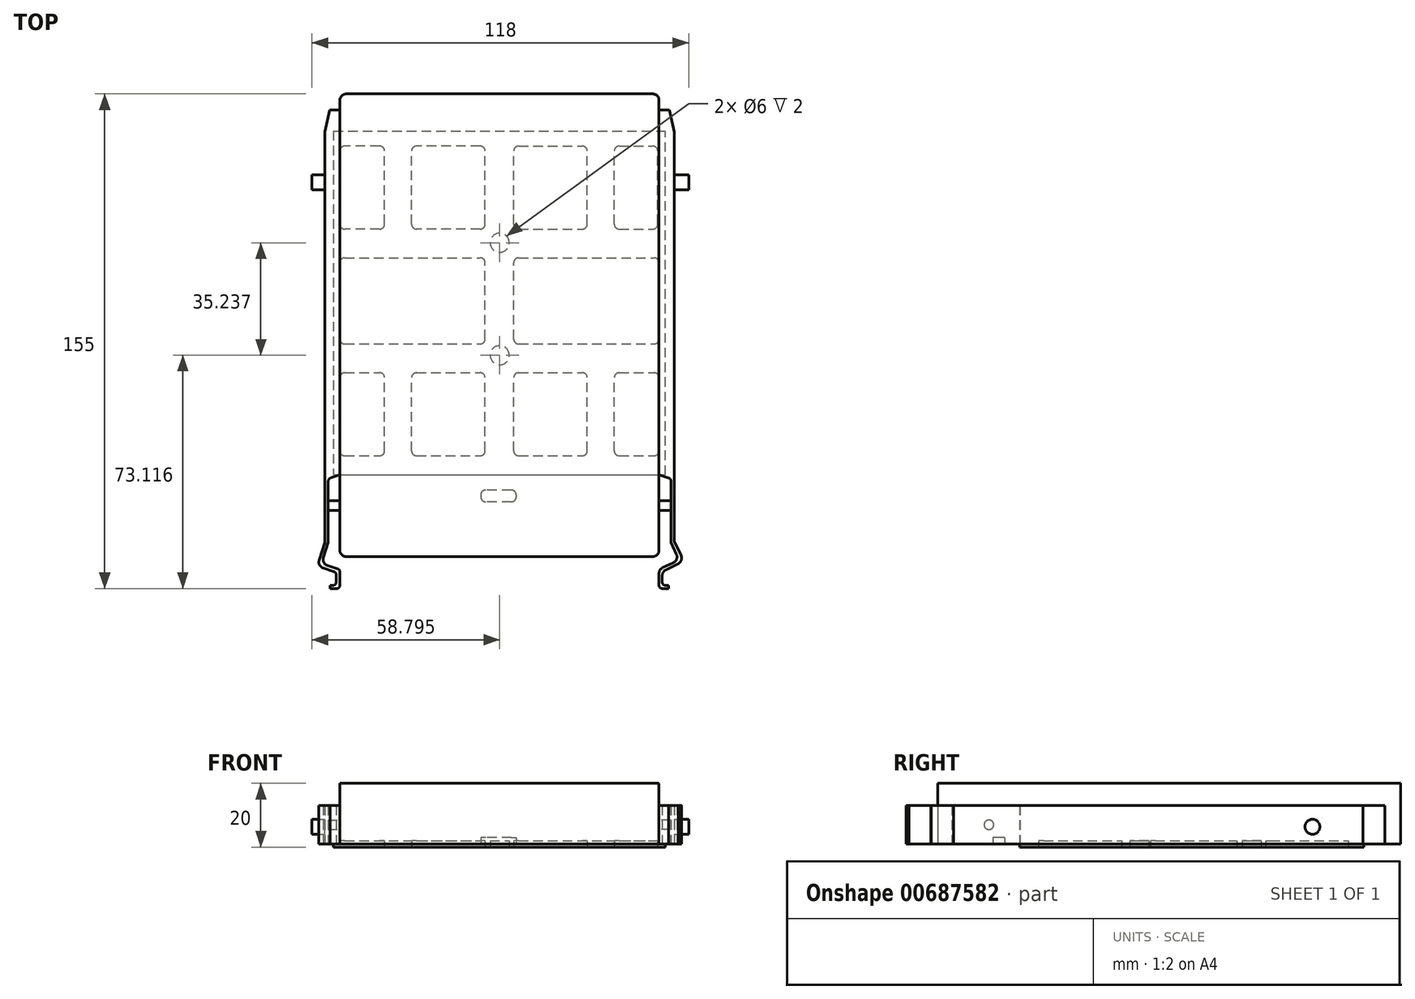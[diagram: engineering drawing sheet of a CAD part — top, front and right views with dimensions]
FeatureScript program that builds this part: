
annotation { "Feature Type Name" : "Feature", "Feature Type Description" : "" }
export const myFeature = defineFeature(function(context is Context, id is Id, definition is map)
    precondition{}
    {
        {
            var Q0;
            Q0=qCreatedBy(makeId("Top.planeOp"),FACE);
            var sketch = newSketch(context, id + "F0", { "sketchPlane" : qUnion([Q0])});
            skLineSegment(sketch, "E0.bottom", {"start": v(-53.24, 65.83) * mm, "end": v(42.76, 65.83) * mm});
            skLineSegment(sketch, "E0.top", {"start": v(-53.24, -79.17) * mm, "end": v(42.76, -79.17) * mm});
            skLineSegment(sketch, "E0.left", {"start": v(-55.24, 63.83) * mm, "end": v(-55.24, -77.17) * mm});
            skLineSegment(sketch, "E0.right", {"start": v(44.76, 63.83) * mm, "end": v(44.76, -77.17) * mm});
            skPoint(sketch, "E1.visualSharp", {"position": v(-55.24, 65.83) * mm});
            skArc(sketch, "E1.filletArc", {"start": v(-53.24, 65.83) * mm, "mid": v(-54.65, 65.24) * mm, "end": v(-55.24, 63.83) * mm});
            skPoint(sketch, "E2.visualSharp", {"position": v(44.76, 65.83) * mm});
            skArc(sketch, "E2.filletArc", {"start": v(44.76, 63.83) * mm, "mid": v(44.18, 65.24) * mm, "end": v(42.76, 65.83) * mm});
            skPoint(sketch, "E3.visualSharp", {"position": v(-55.24, -79.17) * mm});
            skArc(sketch, "E3.filletArc", {"start": v(-55.24, -77.17) * mm, "mid": v(-54.65, -78.59) * mm, "end": v(-53.24, -79.17) * mm});
            skPoint(sketch, "E4.visualSharp", {"position": v(44.76, -79.17) * mm});
            skArc(sketch, "E4.filletArc", {"start": v(42.76, -79.17) * mm, "mid": v(44.18, -78.59) * mm, "end": v(44.76, -77.17) * mm});
            skSolve(sketch);
        }
        {
            var Q0;
            Q0 = qSketchRegion(id + "F0", true);
            extrude(context, id + "F1", {"entities" : qUnion([Q0]), "depth" : 19 * mm, "offsetDistance" : 25 * mm});
        }
        {
            var Q0;
            Q0=makeQuery(id+"F1.opExtrude","SWEPT_FACE",FACE,{"disambiguationData":[OSD([sQuery(id+"F0.wireOp",EDGE,"E0.left")])]});
            var sketch = newSketch(context, id + "F2", { "sketchPlane" : qUnion([Q0])});
            skLineSegment(sketch, "E5", {"start": v(63.17, 0) * mm, "end": v(63.17, 6) * mm});
            skCircle(sketch, "E6", {"center": v(63.17, 6) * mm, "radius": 1.5 * mm});
            skSolve(sketch);
        }
        {
            var Q0;
            Q0 = qSketchRegion(id + "F2", true);
            extrude(context, id + "F3", {"entities" : qUnion([Q0]), "operationType" : NewBodyOperationType.ADD, "depth" : 4 * mm, "offsetDistance" : 25 * mm});
        }
        {
            var Q0;
            Q0=makeQuery(id+"F1.opExtrude","SWEPT_FACE",FACE,{"disambiguationData":[OSD([sQuery(id+"F0.wireOp",EDGE,"E0.right")])]});
            var sketch = newSketch(context, id + "F4", { "sketchPlane" : qUnion([Q0])});
            skLineSegment(sketch, "E7", {"start": v(-63.17, 19) * mm, "end": v(-63.17, 6) * mm});
            skCircle(sketch, "E8", {"center": v(-63.17, 6) * mm, "radius": 1.5 * mm});
            skSolve(sketch);
        }
        {
            var Q0;
            Q0 = qSketchRegion(id + "F4", true);
            extrude(context, id + "F5", {"entities" : qUnion([Q0]), "operationType" : NewBodyOperationType.ADD, "depth" : 4 * mm, "offsetDistance" : 25 * mm});
        }
        {
            var Q0;
            Q0=makeQuery(id+"F1.opExtrude","CAP_FACE",FACE,{"disambiguationData":[OSD([sQuery(id+"F0.wireOp",EDGE,"E0.bottom"),sQuery(id+"F0.wireOp",EDGE,"E0.top"),sQuery(id+"F0.wireOp",EDGE,"E0.left"),sQuery(id+"F0.wireOp",EDGE,"E0.right"),sQuery(id+"F0.wireOp",EDGE,"E1.filletArc"),sQuery(id+"F0.wireOp",EDGE,"E2.filletArc"),sQuery(id+"F0.wireOp",EDGE,"E3.filletArc"),sQuery(id+"F0.wireOp",EDGE,"E4.filletArc")])],"isStart":true});
            var sketch = newSketch(context, id + "F6", { "sketchPlane" : qUnion([Q0])});
            skLineSegment(sketch, "E9", {"start": v(44.76, 84.43) * mm, "end": v(44.76, 89.17) * mm});
            skLineSegment(sketch, "E10", {"start": v(45.76, 89.17) * mm, "end": v(47.76, 89.17) * mm});
            skLineSegment(sketch, "E11", {"start": v(44.76, 88.17) * mm, "end": v(44.76, 84.43) * mm});
            skPoint(sketch, "E12.visualSharp", {"position": v(44.76, 89.17) * mm});
            skArc(sketch, "E12.filletArc", {"start": v(45.76, 89.17) * mm, "mid": v(45.05, 88.88) * mm, "end": v(44.76, 88.17) * mm});
            skLineSegment(sketch, "E13", {"start": v(45.9, 82.63) * mm, "end": v(49.27, 81.02) * mm});
            skPoint(sketch, "E14.visualSharp", {"position": v(44.76, 83.17) * mm});
            skArc(sketch, "E14.filletArc", {"start": v(44.76, 84.43) * mm, "mid": v(45.07, 83.37) * mm, "end": v(45.9, 82.63) * mm});
            skLineSegment(sketch, "E15", {"start": v(50.21, 78.35) * mm, "end": v(48.49, 74.74) * mm});
            skPoint(sketch, "E15.endSnap0", {"position": v(48.49, 81.4) * mm});
            skPoint(sketch, "E16.visualSharp", {"position": v(51.08, 80.15) * mm});
            skArc(sketch, "E16.filletArc", {"start": v(50.21, 78.35) * mm, "mid": v(50.3, 79.88) * mm, "end": v(49.27, 81.02) * mm});
            skLineSegment(sketch, "E17", {"start": v(47.76, 89.17) * mm, "end": v(47.76, 88.17) * mm});
            skLineSegment(sketch, "E18", {"start": v(47.76, 88.17) * mm, "end": v(46.76, 88.17) * mm});
            skLineSegment(sketch, "E19", {"start": v(45.76, 85.1) * mm, "end": v(45.76, 87.17) * mm});
            skLineSegment(sketch, "E20", {"start": v(45.76, 84.43) * mm, "end": v(45.76, 83.87) * mm});
            skLineSegment(sketch, "E21", {"start": v(46.88, 83.32) * mm, "end": v(51.08, 81.24) * mm});
            skArc(sketch, "E22.filletArc", {"start": v(46.76, 88.17) * mm, "mid": v(46.05, 87.88) * mm, "end": v(45.76, 87.17) * mm});
            skPoint(sketch, "E23.newPointB", {"position": v(45.76, 84.43) * mm});
            skArc(sketch, "E23.filletArc", {"start": v(45.76, 85.1) * mm, "mid": v(46.06, 84.05) * mm, "end": v(46.88, 83.32) * mm});
            skLineSegment(sketch, "E24", {"start": v(49.49, 74.3) * mm, "end": v(51.63, 78.78) * mm});
            skLineSegment(sketch, "E25", {"start": v(51.08, 81.24) * mm, "end": v(50.75, 81.41) * mm});
            skPoint(sketch, "E26.visualSharp", {"position": v(52.46, 80.52) * mm});
            skArc(sketch, "E26.filletArc", {"start": v(51.63, 78.78) * mm, "mid": v(51.72, 80.27) * mm, "end": v(50.75, 81.41) * mm});
            skLineSegment(sketch, "E27", {"start": v(48.49, 74.74) * mm, "end": v(48.49, 55.46) * mm});
            skLineSegment(sketch, "E28", {"start": v(49.49, 74.3) * mm, "end": v(49.49, 54.74) * mm});
            skPoint(sketch, "E29.orphan", {"position": v(44.76, 77.17) * mm});
            skPoint(sketch, "E30", {"position": v(44.76, 54.67) * mm});
            skLineSegment(sketch, "E31", {"start": v(47.81, 54.5) * mm, "end": v(44.76, 53.47) * mm});
            skPoint(sketch, "E32.visualSharp", {"position": v(48.49, 54.74) * mm});
            skArc(sketch, "E32.filletArc", {"start": v(47.81, 54.5) * mm, "mid": v(48.3, 54.87) * mm, "end": v(48.49, 55.46) * mm});
            skLineSegment(sketch, "E33", {"start": v(49.49, 54.74) * mm, "end": v(49.49, -53.99) * mm});
            skLineSegment(sketch, "E34", {"start": v(47.99, -60.83) * mm, "end": v(44.76, -60.83) * mm});
            skLineSegment(sketch, "E35", {"start": v(47.99, -60.83) * mm, "end": v(49.49, -53.99) * mm});
            skPoint(sketch, "E36.orphan", {"position": v(49.49, -60.83) * mm});
            skSolve(sketch);
        }
        {
            var Q0;
            Q0 = qSketchRegion(id + "F6", true);
            var Q1;
            Q1=makeQuery(id+"F6.imprint","IMPRINT",FACE,{"disambiguationData":[TD([[makeQuery(id+"F6.imprint","IMPRINT",EDGE,{"derivedFrom":sQuery(id+"F6.wireOp",EDGE,"E10")}),-1.0]])]});
            extrude(context, id + "F7", {"entities" : qUnion([Q0, Q1]), "oppositeDirection" : true, "depth" : 12 * mm, "offsetDistance" : 25 * mm});
        }
        {
            var Q0;
            Q0 = qSketchRegion(id + "F2", true);
            extrude(context, id + "F8", {"entities" : qUnion([Q0]), "operationType" : NewBodyOperationType.ADD, "depth" : 4 * mm, "offsetDistance" : 25 * mm});
        }
        {
            var Q0;
            Q0=makeQuery(id+"F1.opExtrude","CAP_FACE",FACE,{"disambiguationData":[OSD([sQuery(id+"F0.wireOp",EDGE,"E0.bottom"),sQuery(id+"F0.wireOp",EDGE,"E0.top"),sQuery(id+"F0.wireOp",EDGE,"E0.left"),sQuery(id+"F0.wireOp",EDGE,"E0.right"),sQuery(id+"F0.wireOp",EDGE,"E1.filletArc"),sQuery(id+"F0.wireOp",EDGE,"E2.filletArc"),sQuery(id+"F0.wireOp",EDGE,"E3.filletArc"),sQuery(id+"F0.wireOp",EDGE,"E4.filletArc")])],"isStart":true});
            var sketch = newSketch(context, id + "F9", { "sketchPlane" : qUnion([Q0])});
            skLineSegment(sketch, "E37", {"start": v(-52.1, -65.83) * mm, "end": v(-52.1, -60.83) * mm});
            skLineSegment(sketch, "E38", {"start": v(-55.24, -60.83) * mm, "end": v(-58.46, -60.83) * mm});
            skLineSegment(sketch, "E39", {"start": v(-58.46, -60.83) * mm, "end": v(-59.96, -53.99) * mm});
            skLineSegment(sketch, "E40", {"start": v(-59.96, -53.99) * mm, "end": v(-59.96, 74.73) * mm});
            skLineSegment(sketch, "E41", {"start": v(-58.96, 74.73) * mm, "end": v(-58.96, 55.82) * mm});
            skLineSegment(sketch, "E42", {"start": v(-57.92, 54.4) * mm, "end": v(-55.24, 53.53) * mm});
            skPoint(sketch, "E43.visualSharp", {"position": v(-58.96, 54.73) * mm});
            skArc(sketch, "E43.filletArc", {"start": v(-58.96, 55.82) * mm, "mid": v(-58.68, 54.94) * mm, "end": v(-57.92, 54.4) * mm});
            skPoint(sketch, "E44.start.orphan", {"position": v(-58.96, 83.95) * mm});
            skPoint(sketch, "E45", {"position": v(44.69, 89.17) * mm});
            skLineSegment(sketch, "E46", {"start": v(-55.24, 83.17) * mm, "end": v(-55.24, 89.17) * mm});
            skPoint(sketch, "E47.end.orphan", {"position": v(-53.24, 89.17) * mm});
            skLineSegment(sketch, "E48", {"start": v(-56.24, 89.17) * mm, "end": v(-58.24, 89.17) * mm});
            skLineSegment(sketch, "E49", {"start": v(-55.24, 88.17) * mm, "end": v(-55.24, 83.92) * mm});
            skLineSegment(sketch, "E50", {"start": v(-58.96, 74.73) * mm, "end": v(-60.4, 79.52) * mm});
            skLineSegment(sketch, "E51", {"start": v(-59.07, 82.01) * mm, "end": v(-55.95, 82.96) * mm});
            skLineSegment(sketch, "E52", {"start": v(-59.96, 74.73) * mm, "end": v(-61.73, 80.25) * mm});
            skLineSegment(sketch, "E53", {"start": v(-60.43, 82.77) * mm, "end": v(-57.1, 83.83) * mm});
            skLineSegment(sketch, "E54", {"start": v(-56.4, 84.79) * mm, "end": v(-56.4, 87.17) * mm});
            skLineSegment(sketch, "E55", {"start": v(-57.4, 88.17) * mm, "end": v(-58.24, 88.17) * mm});
            skLineSegment(sketch, "E56", {"start": v(-58.24, 88.17) * mm, "end": v(-58.24, 89.17) * mm});
            skPoint(sketch, "E57.orphan", {"position": v(-55.24, 77.17) * mm});
            skPoint(sketch, "E58.visualSharp", {"position": v(-55.24, 89.17) * mm});
            skArc(sketch, "E58.filletArc", {"start": v(-55.24, 88.17) * mm, "mid": v(-55.53, 88.88) * mm, "end": v(-56.24, 89.17) * mm});
            skPoint(sketch, "E59.visualSharp", {"position": v(-56.4, 88.17) * mm});
            skArc(sketch, "E59.filletArc", {"start": v(-56.4, 87.17) * mm, "mid": v(-56.7, 87.88) * mm, "end": v(-57.4, 88.17) * mm});
            skPoint(sketch, "E60.visualSharp", {"position": v(-56.4, 84.05) * mm});
            skArc(sketch, "E60.filletArc", {"start": v(-57.1, 83.83) * mm, "mid": v(-56.6, 84.2) * mm, "end": v(-56.4, 84.79) * mm});
            skPoint(sketch, "E61.visualSharp", {"position": v(-55.24, 83.17) * mm});
            skArc(sketch, "E61.filletArc", {"start": v(-55.95, 82.96) * mm, "mid": v(-55.43, 83.32) * mm, "end": v(-55.24, 83.92) * mm});
            skPoint(sketch, "E62.visualSharp", {"position": v(-60.98, 81.43) * mm});
            skArc(sketch, "E62.filletArc", {"start": v(-59.07, 82.01) * mm, "mid": v(-60.25, 81.04) * mm, "end": v(-60.4, 79.52) * mm});
            skPoint(sketch, "E63.visualSharp", {"position": v(-62.34, 82.16) * mm});
            skArc(sketch, "E63.filletArc", {"start": v(-60.43, 82.77) * mm, "mid": v(-61.6, 81.78) * mm, "end": v(-61.73, 80.25) * mm});
            skSolve(sketch);
        }
        {
            var Q0;
            Q0 = qSketchRegion(id + "F9", true);
            var Q1;
            {var subQ0=sQuery(id+"F9.wireOp",EDGE,"E38");Q1=makeQuery(id+"F9.imprint","IMPRINT",FACE,{"disambiguationData":[TD([[makeQuery(id+"F9.imprint","IMPRINT",EDGE,{"derivedFrom":subQ0}),-1.0]])]});}
            extrude(context, id + "F10", {"entities" : qUnion([Q0, Q1]), "oppositeDirection" : true, "depth" : 12 * mm, "offsetDistance" : 25 * mm});
        }
        {
            var Q0;
            Q0=makeQuery(id+"F1.opExtrude","CAP_FACE",FACE,{"disambiguationData":[OSD([sQuery(id+"F0.wireOp",EDGE,"E0.bottom"),sQuery(id+"F0.wireOp",EDGE,"E0.top"),sQuery(id+"F0.wireOp",EDGE,"E0.left"),sQuery(id+"F0.wireOp",EDGE,"E0.right"),sQuery(id+"F0.wireOp",EDGE,"E1.filletArc"),sQuery(id+"F0.wireOp",EDGE,"E2.filletArc"),sQuery(id+"F0.wireOp",EDGE,"E3.filletArc"),sQuery(id+"F0.wireOp",EDGE,"E4.filletArc")])],"isStart":true});
            var sketch = newSketch(context, id + "F11", { "sketchPlane" : qUnion([Q0])});
            skLineSegment(sketch, "E64", {"start": v(44.76, 53.57) * mm, "end": v(44.76, -54.23) * mm});
            skLineSegment(sketch, "E65", {"start": v(44.76, -54.23) * mm, "end": v(-55.24, -54.23) * mm});
            skLineSegment(sketch, "E66", {"start": v(-55.24, -54.23) * mm, "end": v(-57.24, -54.23) * mm});
            skLineSegment(sketch, "E67", {"start": v(44.76, -54.23) * mm, "end": v(46.76, -54.23) * mm});
            skPoint(sketch, "E68", {"position": v(-55.24, 53.54) * mm});
            skLineSegment(sketch, "E69", {"start": v(-57.24, -54.23) * mm, "end": v(-57.24, 53.54) * mm});
            skLineSegment(sketch, "E70", {"start": v(-57.24, 53.54) * mm, "end": v(46.76, 53.54) * mm});
            skLineSegment(sketch, "E71", {"start": v(46.76, 53.54) * mm, "end": v(46.76, -54.23) * mm});
            skSolve(sketch);
        }
        {
            var Q0;
            Q0 = qSketchRegion(id + "F11", true);
            extrude(context, id + "F12", {"entities" : qUnion([Q0]), "operationType" : NewBodyOperationType.ADD, "depth" : 1 * mm, "offsetDistance" : 25 * mm});
        }
        {
            var Q0;
            Q0=makeQuery(id+"F12.opExtrude","CAP_FACE",FACE,{"disambiguationData":[OSD([sQuery(id+"F11.wireOp",EDGE,"E65"),sQuery(id+"F11.wireOp",EDGE,"E66"),sQuery(id+"F11.wireOp",EDGE,"E67"),sQuery(id+"F11.wireOp",EDGE,"E69"),sQuery(id+"F11.wireOp",EDGE,"E70"),sQuery(id+"F11.wireOp",EDGE,"E71")])],"isStart":false});
            var sketch = newSketch(context, id + "F13", { "sketchPlane" : qUnion([Q0])});
            skLineSegment(sketch, "E72.bottom", {"start": v(-53.74, 47.54) * mm, "end": v(-42.74, 47.54) * mm});
            skLineSegment(sketch, "E72.top", {"start": v(-53.74, 21.54) * mm, "end": v(-42.74, 21.54) * mm});
            skLineSegment(sketch, "E72.left", {"start": v(-55.24, 46.04) * mm, "end": v(-55.24, 23.04) * mm});
            skLineSegment(sketch, "E72.right", {"start": v(-41.24, 46.04) * mm, "end": v(-41.24, 23.04) * mm});
            skPoint(sketch, "E73", {"position": v(-51.73, 53.54) * mm});
            skPoint(sketch, "E74.visualSharp", {"position": v(-55.24, 47.54) * mm});
            skArc(sketch, "E74.filletArc", {"start": v(-53.74, 47.54) * mm, "mid": v(-54.8, 47.1) * mm, "end": v(-55.24, 46.04) * mm});
            skPoint(sketch, "E75.visualSharp", {"position": v(-41.24, 47.54) * mm});
            skArc(sketch, "E75.filletArc", {"start": v(-41.24, 46.04) * mm, "mid": v(-41.68, 47.1) * mm, "end": v(-42.74, 47.54) * mm});
            skPoint(sketch, "E76.visualSharp", {"position": v(-41.24, 21.54) * mm});
            skArc(sketch, "E76.filletArc", {"start": v(-42.74, 21.54) * mm, "mid": v(-41.68, 21.98) * mm, "end": v(-41.24, 23.04) * mm});
            skPoint(sketch, "E77.visualSharp", {"position": v(-55.24, 21.54) * mm});
            skArc(sketch, "E77.filletArc", {"start": v(-55.24, 23.04) * mm, "mid": v(-54.8, 21.98) * mm, "end": v(-53.74, 21.54) * mm});
            skSolve(sketch);
        }
        {
            var Q0;
            Q0 = qSketchRegion(id + "F13", true);
            extrude(context, id + "F14", {"entities" : qUnion([Q0]), "operationType" : NewBodyOperationType.REMOVE, "oppositeDirection" : true, "depth" : 2 * mm, "offsetDistance" : 25 * mm});
        }
        {
            var Q0;
            Q0=makeQuery(id+"F12.opExtrude","CAP_FACE",FACE,{"disambiguationData":[OSD([sQuery(id+"F11.wireOp",EDGE,"E65"),sQuery(id+"F11.wireOp",EDGE,"E66"),sQuery(id+"F11.wireOp",EDGE,"E67"),sQuery(id+"F11.wireOp",EDGE,"E69"),sQuery(id+"F11.wireOp",EDGE,"E70"),sQuery(id+"F11.wireOp",EDGE,"E71")])],"isStart":false});
            var sketch = newSketch(context, id + "F15", { "sketchPlane" : qUnion([Q0])});
            skLineSegment(sketch, "E78.bottom", {"start": v(-31.24, 47.54) * mm, "end": v(-11.24, 47.54) * mm});
            skLineSegment(sketch, "E78.top", {"start": v(-31.24, 21.54) * mm, "end": v(-11.24, 21.54) * mm});
            skLineSegment(sketch, "E78.left", {"start": v(-32.74, 46.04) * mm, "end": v(-32.74, 23.04) * mm});
            skLineSegment(sketch, "E78.right", {"start": v(-9.74, 46.04) * mm, "end": v(-9.74, 23.04) * mm});
            skPoint(sketch, "E79.visualSharp", {"position": v(-32.74, 47.54) * mm});
            skArc(sketch, "E79.filletArc", {"start": v(-31.24, 47.54) * mm, "mid": v(-32.3, 47.1) * mm, "end": v(-32.74, 46.04) * mm});
            skPoint(sketch, "E80.visualSharp", {"position": v(-9.74, 47.54) * mm});
            skArc(sketch, "E80.filletArc", {"start": v(-9.74, 46.04) * mm, "mid": v(-10.18, 47.1) * mm, "end": v(-11.24, 47.54) * mm});
            skPoint(sketch, "E81.visualSharp", {"position": v(-9.74, 21.54) * mm});
            skArc(sketch, "E81.filletArc", {"start": v(-11.24, 21.54) * mm, "mid": v(-10.18, 21.98) * mm, "end": v(-9.74, 23.04) * mm});
            skPoint(sketch, "E82.visualSharp", {"position": v(-32.74, 21.54) * mm});
            skArc(sketch, "E82.filletArc", {"start": v(-32.74, 23.04) * mm, "mid": v(-32.3, 21.98) * mm, "end": v(-31.24, 21.54) * mm});
            skSolve(sketch);
        }
        {
            var Q0;
            Q0 = qSketchRegion(id + "F15", true);
            extrude(context, id + "F16", {"entities" : qUnion([Q0]), "operationType" : NewBodyOperationType.REMOVE, "oppositeDirection" : true, "depth" : 2 * mm, "offsetDistance" : 25 * mm});
        }
        {
            var Q0;
            Q0=makeQuery(id+"F12.opExtrude","CAP_FACE",FACE,{"disambiguationData":[OSD([sQuery(id+"F11.wireOp",EDGE,"E65"),sQuery(id+"F11.wireOp",EDGE,"E66"),sQuery(id+"F11.wireOp",EDGE,"E67"),sQuery(id+"F11.wireOp",EDGE,"E69"),sQuery(id+"F11.wireOp",EDGE,"E70"),sQuery(id+"F11.wireOp",EDGE,"E71")])],"isStart":false});
            var sketch = newSketch(context, id + "F17", { "sketchPlane" : qUnion([Q0])});
            skLineSegment(sketch, "E83.bottom", {"start": v(0.76, 47.54) * mm, "end": v(20.76, 47.54) * mm});
            skLineSegment(sketch, "E83.top", {"start": v(0.76, 21.54) * mm, "end": v(20.76, 21.54) * mm});
            skLineSegment(sketch, "E83.left", {"start": v(-0.74, 46.04) * mm, "end": v(-0.74, 23.04) * mm});
            skLineSegment(sketch, "E83.right", {"start": v(22.26, 46.04) * mm, "end": v(22.26, 23.04) * mm});
            skPoint(sketch, "E84.visualSharp", {"position": v(-0.74, 47.54) * mm});
            skArc(sketch, "E84.filletArc", {"start": v(0.76, 47.54) * mm, "mid": v(-0.3, 47.1) * mm, "end": v(-0.74, 46.04) * mm});
            skPoint(sketch, "E85.visualSharp", {"position": v(22.26, 47.54) * mm});
            skArc(sketch, "E85.filletArc", {"start": v(22.26, 46.04) * mm, "mid": v(21.82, 47.1) * mm, "end": v(20.76, 47.54) * mm});
            skPoint(sketch, "E86.visualSharp", {"position": v(22.26, 21.54) * mm});
            skArc(sketch, "E86.filletArc", {"start": v(20.76, 21.54) * mm, "mid": v(21.82, 21.98) * mm, "end": v(22.26, 23.04) * mm});
            skPoint(sketch, "E87.visualSharp", {"position": v(-0.74, 21.54) * mm});
            skArc(sketch, "E87.filletArc", {"start": v(-0.74, 23.04) * mm, "mid": v(-0.3, 21.98) * mm, "end": v(0.76, 21.54) * mm});
            skSolve(sketch);
        }
        {
            var Q0;
            Q0 = qSketchRegion(id + "F17", true);
            extrude(context, id + "F18", {"entities" : qUnion([Q0]), "operationType" : NewBodyOperationType.REMOVE, "oppositeDirection" : true, "depth" : 2 * mm, "offsetDistance" : 25 * mm});
        }
        {
            var Q0;
            Q0=makeQuery(id+"F12.opExtrude","CAP_FACE",FACE,{"disambiguationData":[OSD([sQuery(id+"F11.wireOp",EDGE,"E65"),sQuery(id+"F11.wireOp",EDGE,"E66"),sQuery(id+"F11.wireOp",EDGE,"E67"),sQuery(id+"F11.wireOp",EDGE,"E69"),sQuery(id+"F11.wireOp",EDGE,"E70"),sQuery(id+"F11.wireOp",EDGE,"E71")])],"isStart":false});
            var sketch = newSketch(context, id + "F19", { "sketchPlane" : qUnion([Q0])});
            skLineSegment(sketch, "E88.bottom", {"start": v(32.26, 47.54) * mm, "end": v(43.26, 47.54) * mm});
            skLineSegment(sketch, "E88.top", {"start": v(32.26, 21.54) * mm, "end": v(43.26, 21.54) * mm});
            skLineSegment(sketch, "E88.left", {"start": v(30.76, 46.04) * mm, "end": v(30.76, 23.04) * mm});
            skLineSegment(sketch, "E88.right", {"start": v(44.76, 46.04) * mm, "end": v(44.76, 23.04) * mm});
            skPoint(sketch, "E89.visualSharp", {"position": v(30.76, 47.54) * mm});
            skArc(sketch, "E89.filletArc", {"start": v(32.26, 47.54) * mm, "mid": v(31.2, 47.1) * mm, "end": v(30.76, 46.04) * mm});
            skPoint(sketch, "E90.visualSharp", {"position": v(44.76, 47.54) * mm});
            skArc(sketch, "E90.filletArc", {"start": v(44.76, 46.04) * mm, "mid": v(44.32, 47.1) * mm, "end": v(43.26, 47.54) * mm});
            skPoint(sketch, "E91.visualSharp", {"position": v(30.76, 21.54) * mm});
            skArc(sketch, "E91.filletArc", {"start": v(30.76, 23.04) * mm, "mid": v(31.2, 21.98) * mm, "end": v(32.26, 21.54) * mm});
            skPoint(sketch, "E92.visualSharp", {"position": v(44.76, 21.54) * mm});
            skArc(sketch, "E92.filletArc", {"start": v(43.26, 21.54) * mm, "mid": v(44.32, 21.98) * mm, "end": v(44.76, 23.04) * mm});
            skSolve(sketch);
        }
        {
            var Q0;
            Q0 = qSketchRegion(id + "F19", true);
            extrude(context, id + "F20", {"entities" : qUnion([Q0]), "operationType" : NewBodyOperationType.REMOVE, "oppositeDirection" : true, "depth" : 2 * mm, "offsetDistance" : 25 * mm});
        }
        {
            var Q0;
            Q0=makeQuery(id+"F12.opExtrude","CAP_FACE",FACE,{"disambiguationData":[OSD([sQuery(id+"F11.wireOp",EDGE,"E65"),sQuery(id+"F11.wireOp",EDGE,"E66"),sQuery(id+"F11.wireOp",EDGE,"E67"),sQuery(id+"F11.wireOp",EDGE,"E69"),sQuery(id+"F11.wireOp",EDGE,"E70"),sQuery(id+"F11.wireOp",EDGE,"E71")])],"isStart":false});
            var sketch = newSketch(context, id + "F21", { "sketchPlane" : qUnion([Q0])});
            skPoint(sketch, "E93.oppositeSnap0", {"position": v(-12.3, 24.1) * mm});
            skPoint(sketch, "E94.visualSharp", {"position": v(-55.24, 12.54) * mm});
            skPoint(sketch, "E95.visualSharp", {"position": v(-12.3, 12.54) * mm});
            skPoint(sketch, "E96.visualSharp", {"position": v(-12.3, -14.46) * mm});
            skPoint(sketch, "E97.visualSharp", {"position": v(-55.24, -14.46) * mm});
            skLineSegment(sketch, "E98.bottom", {"start": v(-53.74, 12.54) * mm, "end": v(-11.24, 12.54) * mm});
            skLineSegment(sketch, "E98.top", {"start": v(-53.74, -14.47) * mm, "end": v(-11.24, -14.47) * mm});
            skLineSegment(sketch, "E98.left", {"start": v(-55.24, 11.04) * mm, "end": v(-55.24, -12.97) * mm});
            skLineSegment(sketch, "E98.right", {"start": v(-9.74, 11.04) * mm, "end": v(-9.74, -12.97) * mm});
            skArc(sketch, "E99.filletArc", {"start": v(-53.74, 12.54) * mm, "mid": v(-54.8, 12.1) * mm, "end": v(-55.24, 11.04) * mm});
            skPoint(sketch, "E100.visualSharp", {"position": v(-9.74, 12.54) * mm});
            skArc(sketch, "E100.filletArc", {"start": v(-9.74, 11.04) * mm, "mid": v(-10.18, 12.1) * mm, "end": v(-11.24, 12.54) * mm});
            skPoint(sketch, "E101.visualSharp", {"position": v(-9.74, -14.47) * mm});
            skArc(sketch, "E101.filletArc", {"start": v(-11.24, -14.47) * mm, "mid": v(-10.18, -14.03) * mm, "end": v(-9.74, -12.97) * mm});
            skPoint(sketch, "E102.visualSharp", {"position": v(-55.24, -14.47) * mm});
            skArc(sketch, "E102.filletArc", {"start": v(-55.24, -12.97) * mm, "mid": v(-54.8, -14.03) * mm, "end": v(-53.74, -14.47) * mm});
            skSolve(sketch);
        }
        {
            var Q0;
            Q0 = qSketchRegion(id + "F21", true);
            extrude(context, id + "F22", {"entities" : qUnion([Q0]), "operationType" : NewBodyOperationType.REMOVE, "oppositeDirection" : true, "depth" : 2 * mm, "offsetDistance" : 25 * mm});
        }
        {
            var Q0;
            Q0=makeQuery(id+"F12.opExtrude","CAP_FACE",FACE,{"disambiguationData":[OSD([sQuery(id+"F11.wireOp",EDGE,"E65"),sQuery(id+"F11.wireOp",EDGE,"E66"),sQuery(id+"F11.wireOp",EDGE,"E67"),sQuery(id+"F11.wireOp",EDGE,"E69"),sQuery(id+"F11.wireOp",EDGE,"E70"),sQuery(id+"F11.wireOp",EDGE,"E71")])],"isStart":false});
            var sketch = newSketch(context, id + "F23", { "sketchPlane" : qUnion([Q0])});
            skLineSegment(sketch, "E103.bottom", {"start": v(0.76, 12.54) * mm, "end": v(43.26, 12.54) * mm});
            skLineSegment(sketch, "E103.top", {"start": v(0.76, -14.46) * mm, "end": v(43.26, -14.46) * mm});
            skLineSegment(sketch, "E103.left", {"start": v(-0.74, 11.04) * mm, "end": v(-0.74, -12.96) * mm});
            skLineSegment(sketch, "E103.right", {"start": v(44.76, 11.04) * mm, "end": v(44.76, -12.96) * mm});
            skPoint(sketch, "E104.visualSharp", {"position": v(-0.74, 12.54) * mm});
            skArc(sketch, "E104.filletArc", {"start": v(0.76, 12.54) * mm, "mid": v(-0.3, 12.1) * mm, "end": v(-0.74, 11.04) * mm});
            skPoint(sketch, "E105.visualSharp", {"position": v(-0.74, -14.46) * mm});
            skArc(sketch, "E105.filletArc", {"start": v(-0.74, -12.96) * mm, "mid": v(-0.3, -14.02) * mm, "end": v(0.76, -14.46) * mm});
            skPoint(sketch, "E106.visualSharp", {"position": v(44.76, 12.54) * mm});
            skArc(sketch, "E106.filletArc", {"start": v(44.76, 11.04) * mm, "mid": v(44.32, 12.1) * mm, "end": v(43.26, 12.54) * mm});
            skPoint(sketch, "E107.visualSharp", {"position": v(44.76, -14.46) * mm});
            skArc(sketch, "E107.filletArc", {"start": v(43.26, -14.46) * mm, "mid": v(44.32, -14.02) * mm, "end": v(44.76, -12.96) * mm});
            skSolve(sketch);
        }
        {
            var Q0;
            Q0 = qSketchRegion(id + "F23", true);
            extrude(context, id + "F24", {"entities" : qUnion([Q0]), "operationType" : NewBodyOperationType.REMOVE, "oppositeDirection" : true, "depth" : 2 * mm, "offsetDistance" : 25 * mm});
        }
        {
            var Q0;
            Q0=makeQuery(id+"F12.opExtrude","CAP_FACE",FACE,{"disambiguationData":[OSD([sQuery(id+"F11.wireOp",EDGE,"E65"),sQuery(id+"F11.wireOp",EDGE,"E66"),sQuery(id+"F11.wireOp",EDGE,"E67"),sQuery(id+"F11.wireOp",EDGE,"E69"),sQuery(id+"F11.wireOp",EDGE,"E70"),sQuery(id+"F11.wireOp",EDGE,"E71")])],"isStart":false});
            var sketch = newSketch(context, id + "F25", { "sketchPlane" : qUnion([Q0])});
            skPoint(sketch, "E108.firstSnap0", {"position": v(-9.74, -9.02) * mm});
            skPoint(sketch, "E108.oppositeSnap0", {"position": v(-32.74, 12.68) * mm});
            skLineSegment(sketch, "E108.bottom", {"start": v(-11.24, -23.47) * mm, "end": v(-31.24, -23.47) * mm});
            skLineSegment(sketch, "E108.top", {"start": v(-11.24, -49.47) * mm, "end": v(-31.24, -49.47) * mm});
            skLineSegment(sketch, "E108.left", {"start": v(-9.74, -24.97) * mm, "end": v(-9.74, -47.97) * mm});
            skLineSegment(sketch, "E108.right", {"start": v(-32.74, -24.97) * mm, "end": v(-32.74, -47.97) * mm});
            skPoint(sketch, "E109.visualSharp", {"position": v(-32.74, -23.47) * mm});
            skArc(sketch, "E109.filletArc", {"start": v(-31.24, -23.47) * mm, "mid": v(-32.3, -23.91) * mm, "end": v(-32.74, -24.97) * mm});
            skPoint(sketch, "E110.visualSharp", {"position": v(-9.74, -23.47) * mm});
            skArc(sketch, "E110.filletArc", {"start": v(-9.74, -24.97) * mm, "mid": v(-10.18, -23.91) * mm, "end": v(-11.24, -23.47) * mm});
            skPoint(sketch, "E111.visualSharp", {"position": v(-32.74, -49.47) * mm});
            skArc(sketch, "E111.filletArc", {"start": v(-32.74, -47.97) * mm, "mid": v(-32.3, -49.03) * mm, "end": v(-31.24, -49.47) * mm});
            skPoint(sketch, "E112.visualSharp", {"position": v(-9.74, -49.47) * mm});
            skArc(sketch, "E112.filletArc", {"start": v(-11.24, -49.47) * mm, "mid": v(-10.18, -49.03) * mm, "end": v(-9.74, -47.97) * mm});
            skSolve(sketch);
        }
        {
            var Q0;
            Q0 = qSketchRegion(id + "F25", true);
            extrude(context, id + "F26", {"entities" : qUnion([Q0]), "operationType" : NewBodyOperationType.REMOVE, "oppositeDirection" : true, "depth" : 2 * mm, "offsetDistance" : 25 * mm});
        }
        {
            var Q0;
            Q0=makeQuery(id+"F12.opExtrude","CAP_FACE",FACE,{"disambiguationData":[OSD([sQuery(id+"F11.wireOp",EDGE,"E65"),sQuery(id+"F11.wireOp",EDGE,"E66"),sQuery(id+"F11.wireOp",EDGE,"E67"),sQuery(id+"F11.wireOp",EDGE,"E69"),sQuery(id+"F11.wireOp",EDGE,"E70"),sQuery(id+"F11.wireOp",EDGE,"E71")])],"isStart":false});
            var sketch = newSketch(context, id + "F27", { "sketchPlane" : qUnion([Q0])});
            skLineSegment(sketch, "E113.bottom", {"start": v(0.76, -23.47) * mm, "end": v(20.76, -23.47) * mm});
            skLineSegment(sketch, "E113.top", {"start": v(0.76, -49.47) * mm, "end": v(20.76, -49.47) * mm});
            skLineSegment(sketch, "E113.left", {"start": v(-0.74, -24.97) * mm, "end": v(-0.74, -47.97) * mm});
            skLineSegment(sketch, "E113.right", {"start": v(22.26, -24.97) * mm, "end": v(22.26, -47.97) * mm});
            skPoint(sketch, "E114.visualSharp", {"position": v(22.26, -49.47) * mm});
            skArc(sketch, "E114.filletArc", {"start": v(20.76, -49.47) * mm, "mid": v(21.82, -49.03) * mm, "end": v(22.26, -47.97) * mm});
            skPoint(sketch, "E115.visualSharp", {"position": v(-0.74, -49.47) * mm});
            skArc(sketch, "E115.filletArc", {"start": v(-0.74, -47.97) * mm, "mid": v(-0.3, -49.03) * mm, "end": v(0.76, -49.47) * mm});
            skPoint(sketch, "E116.visualSharp", {"position": v(-0.74, -23.47) * mm});
            skArc(sketch, "E116.filletArc", {"start": v(0.76, -23.47) * mm, "mid": v(-0.3, -23.91) * mm, "end": v(-0.74, -24.97) * mm});
            skPoint(sketch, "E117.visualSharp", {"position": v(22.26, -23.47) * mm});
            skArc(sketch, "E117.filletArc", {"start": v(22.26, -24.97) * mm, "mid": v(21.82, -23.91) * mm, "end": v(20.76, -23.47) * mm});
            skSolve(sketch);
        }
        {
            var Q0;
            Q0 = qSketchRegion(id + "F27", true);
            extrude(context, id + "F28", {"entities" : qUnion([Q0]), "operationType" : NewBodyOperationType.REMOVE, "oppositeDirection" : true, "depth" : 2 * mm, "offsetDistance" : 25 * mm});
        }
        {
            var Q0;
            Q0=makeQuery(id+"F12.opExtrude","CAP_FACE",FACE,{"disambiguationData":[OSD([sQuery(id+"F11.wireOp",EDGE,"E65"),sQuery(id+"F11.wireOp",EDGE,"E66"),sQuery(id+"F11.wireOp",EDGE,"E67"),sQuery(id+"F11.wireOp",EDGE,"E69"),sQuery(id+"F11.wireOp",EDGE,"E70"),sQuery(id+"F11.wireOp",EDGE,"E71")])],"isStart":false});
            var sketch = newSketch(context, id + "F29", { "sketchPlane" : qUnion([Q0])});
            skPoint(sketch, "E118.oppositeSnap0", {"position": v(44.32, -14.02) * mm});
            skLineSegment(sketch, "E118.bottom", {"start": v(32.26, -23.47) * mm, "end": v(42.82, -23.47) * mm});
            skLineSegment(sketch, "E118.top", {"start": v(32.26, -49.47) * mm, "end": v(42.82, -49.47) * mm});
            skLineSegment(sketch, "E118.left", {"start": v(30.76, -24.97) * mm, "end": v(30.76, -47.97) * mm});
            skLineSegment(sketch, "E118.right", {"start": v(44.32, -24.97) * mm, "end": v(44.32, -47.97) * mm});
            skPoint(sketch, "E119.visualSharp", {"position": v(44.32, -49.47) * mm});
            skArc(sketch, "E119.filletArc", {"start": v(42.82, -49.47) * mm, "mid": v(43.88, -49.03) * mm, "end": v(44.32, -47.97) * mm});
            skPoint(sketch, "E120.visualSharp", {"position": v(30.76, -49.47) * mm});
            skArc(sketch, "E120.filletArc", {"start": v(30.76, -47.97) * mm, "mid": v(31.2, -49.03) * mm, "end": v(32.26, -49.47) * mm});
            skPoint(sketch, "E121.visualSharp", {"position": v(30.76, -23.47) * mm});
            skArc(sketch, "E121.filletArc", {"start": v(32.26, -23.47) * mm, "mid": v(31.2, -23.91) * mm, "end": v(30.76, -24.97) * mm});
            skPoint(sketch, "E122.visualSharp", {"position": v(44.32, -23.47) * mm});
            skArc(sketch, "E122.filletArc", {"start": v(44.32, -24.97) * mm, "mid": v(43.88, -23.91) * mm, "end": v(42.82, -23.47) * mm});
            skSolve(sketch);
        }
        {
            var Q0;
            Q0 = qSketchRegion(id + "F29", true);
            extrude(context, id + "F30", {"entities" : qUnion([Q0]), "operationType" : NewBodyOperationType.REMOVE, "oppositeDirection" : true, "depth" : 2 * mm, "offsetDistance" : 25 * mm});
        }
        {
            var Q0;
            Q0=makeQuery(id+"F12.opExtrude","CAP_FACE",FACE,{"disambiguationData":[OSD([sQuery(id+"F11.wireOp",EDGE,"E65"),sQuery(id+"F11.wireOp",EDGE,"E66"),sQuery(id+"F11.wireOp",EDGE,"E67"),sQuery(id+"F11.wireOp",EDGE,"E69"),sQuery(id+"F11.wireOp",EDGE,"E70"),sQuery(id+"F11.wireOp",EDGE,"E71")])],"isStart":false});
            var sketch = newSketch(context, id + "F31", { "sketchPlane" : qUnion([Q0])});
            skLineSegment(sketch, "E123.bottom", {"start": v(-42.74, -23.47) * mm, "end": v(-53.74, -23.47) * mm});
            skLineSegment(sketch, "E123.top", {"start": v(-42.74, -49.47) * mm, "end": v(-53.74, -49.47) * mm});
            skLineSegment(sketch, "E123.left", {"start": v(-41.24, -24.97) * mm, "end": v(-41.24, -47.97) * mm});
            skLineSegment(sketch, "E123.right", {"start": v(-55.24, -24.97) * mm, "end": v(-55.24, -47.97) * mm});
            skPoint(sketch, "E124.visualSharp", {"position": v(-41.24, -49.47) * mm});
            skArc(sketch, "E124.filletArc", {"start": v(-42.74, -49.47) * mm, "mid": v(-41.68, -49.03) * mm, "end": v(-41.24, -47.97) * mm});
            skPoint(sketch, "E125.visualSharp", {"position": v(-41.24, -23.47) * mm});
            skArc(sketch, "E125.filletArc", {"start": v(-41.24, -24.97) * mm, "mid": v(-41.68, -23.91) * mm, "end": v(-42.74, -23.47) * mm});
            skPoint(sketch, "E126.visualSharp", {"position": v(-55.24, -23.47) * mm});
            skArc(sketch, "E126.filletArc", {"start": v(-53.74, -23.47) * mm, "mid": v(-54.8, -23.91) * mm, "end": v(-55.24, -24.97) * mm});
            skPoint(sketch, "E127.visualSharp", {"position": v(-55.24, -49.47) * mm});
            skArc(sketch, "E127.filletArc", {"start": v(-55.24, -47.97) * mm, "mid": v(-54.8, -49.03) * mm, "end": v(-53.74, -49.47) * mm});
            skSolve(sketch);
        }
        {
            var Q0;
            Q0 = qSketchRegion(id + "F31", true);
            extrude(context, id + "F32", {"entities" : qUnion([Q0]), "operationType" : NewBodyOperationType.REMOVE, "oppositeDirection" : true, "depth" : 2 * mm, "offsetDistance" : 25 * mm});
        }
        {
            var Q0;
            Q0=makeQuery(id+"F12.opExtrude","CAP_FACE",FACE,{"disambiguationData":[OSD([sQuery(id+"F11.wireOp",EDGE,"E65"),sQuery(id+"F11.wireOp",EDGE,"E66"),sQuery(id+"F11.wireOp",EDGE,"E67"),sQuery(id+"F11.wireOp",EDGE,"E69"),sQuery(id+"F11.wireOp",EDGE,"E70"),sQuery(id+"F11.wireOp",EDGE,"E71")])],"isStart":false});
            var sketch = newSketch(context, id + "F33", { "sketchPlane" : qUnion([Q0])});
            skCircle(sketch, "E128", {"center": v(-5.17, -19.18) * mm, "radius": 3 * mm});
            skSolve(sketch);
        }
        {
            var Q0;
            Q0 = qSketchRegion(id + "F33", true);
            extrude(context, id + "F34", {"entities" : qUnion([Q0]), "operationType" : NewBodyOperationType.REMOVE, "oppositeDirection" : true, "depth" : 2 * mm, "offsetDistance" : 25 * mm});
        }
        {
            var Q0;
            Q0=makeQuery(id+"F12.opExtrude","CAP_FACE",FACE,{"disambiguationData":[OSD([sQuery(id+"F11.wireOp",EDGE,"E65"),sQuery(id+"F11.wireOp",EDGE,"E66"),sQuery(id+"F11.wireOp",EDGE,"E67"),sQuery(id+"F11.wireOp",EDGE,"E69"),sQuery(id+"F11.wireOp",EDGE,"E70"),sQuery(id+"F11.wireOp",EDGE,"E71")])],"isStart":false});
            var sketch = newSketch(context, id + "F35", { "sketchPlane" : qUnion([Q0])});
            skCircle(sketch, "E129", {"center": v(-5.17, 16.05) * mm, "radius": 3 * mm});
            skPoint(sketch, "E130.orphan", {"position": v(-5.17, -19.18) * mm});
            skSolve(sketch);
        }
        {
            var Q0;
            Q0 = qSketchRegion(id + "F35", true);
            extrude(context, id + "F36", {"entities" : qUnion([Q0]), "operationType" : NewBodyOperationType.REMOVE, "oppositeDirection" : true, "depth" : 2 * mm, "offsetDistance" : 25 * mm});
        }
        {
            var Q0;
            {var subQ0=sQuery(id+"F0.wireOp",EDGE,"E0.right");var subQ1=sQuery(id+"F0.wireOp",EDGE,"E0.left");var subQ2=sQuery(id+"F0.wireOp",EDGE,"E3.filletArc");var subQ4=sQuery(id+"F0.wireOp",EDGE,"E0.top");var subQ5=sQuery(id+"F0.wireOp",EDGE,"E4.filletArc");Q0=makeQuery(id+"F12.boolean.opBoolean","SPLIT",FACE,{"disambiguationData":[TD([makeQuery(id+"F1.opExtrude","SWEPT_FACE",FACE,{"disambiguationData":[OSD([subQ4])]})])],"derivedFrom":makeQuery(id+"F1.opExtrude","CAP_FACE",FACE,{"disambiguationData":[OSD([sQuery(id+"F0.wireOp",EDGE,"E0.bottom"),subQ4,subQ1,subQ0,sQuery(id+"F0.wireOp",EDGE,"E1.filletArc"),sQuery(id+"F0.wireOp",EDGE,"E2.filletArc"),subQ2,subQ5])],"isStart":true})});}
            var sketch = newSketch(context, id + "F37", { "sketchPlane" : qUnion([Q0])});
            skLineSegment(sketch, "E131.bottom", {"start": v(-1.5, 58.3) * mm, "end": v(-9.58, 58.3) * mm});
            skLineSegment(sketch, "E131.top", {"start": v(-1.5, 61.98) * mm, "end": v(-9.58, 61.98) * mm});
            skLineSegment(sketch, "E131.left", {"start": v(0, 59.8) * mm, "end": v(0, 60.48) * mm});
            skLineSegment(sketch, "E131.right", {"start": v(-11.08, 59.8) * mm, "end": v(-11.08, 60.48) * mm});
            skPoint(sketch, "E132.visualSharp", {"position": v(0, 58.3) * mm});
            skArc(sketch, "E132.filletArc", {"start": v(-1.5, 58.3) * mm, "mid": v(-0.44, 58.75) * mm, "end": v(0, 59.8) * mm});
            skPoint(sketch, "E133.visualSharp", {"position": v(-11.08, 58.3) * mm});
            skArc(sketch, "E133.filletArc", {"start": v(-11.08, 59.8) * mm, "mid": v(-10.64, 58.75) * mm, "end": v(-9.58, 58.3) * mm});
            skPoint(sketch, "E134.visualSharp", {"position": v(0, 61.98) * mm});
            skArc(sketch, "E134.filletArc", {"start": v(0, 60.48) * mm, "mid": v(-0.44, 61.54) * mm, "end": v(-1.5, 61.98) * mm});
            skPoint(sketch, "E135.visualSharp", {"position": v(-11.08, 61.98) * mm});
            skArc(sketch, "E135.filletArc", {"start": v(-9.58, 61.98) * mm, "mid": v(-10.64, 61.54) * mm, "end": v(-11.08, 60.48) * mm});
            skSolve(sketch);
        }
        {
            var Q0;
            Q0 = qSketchRegion(id + "F37", true);
            extrude(context, id + "F38", {"entities" : qUnion([Q0]), "operationType" : NewBodyOperationType.REMOVE, "oppositeDirection" : true, "depth" : 2 * mm, "offsetDistance" : 25 * mm});
        }
        {
            var Q0;
            Q0=makeQuery(id+"F10.opExtrude","SWEPT_FACE",FACE,{"disambiguationData":[OSD([sQuery(id+"F9.wireOp",EDGE,"E40")])]});
            var sketch = newSketch(context, id + "F39", { "sketchPlane" : qUnion([Q0])});
            skCircle(sketch, "E136", {"center": v(-38.17, 5.36) * mm, "radius": 2.34 * mm});
            skSolve(sketch);
        }
        {
            var Q0;
            Q0 = qSketchRegion(id + "F39", true);
            extrude(context, id + "F40", {"entities" : qUnion([Q0]), "operationType" : NewBodyOperationType.ADD, "depth" : 4 * mm, "offsetDistance" : 25 * mm, "hasSecondDirection" : true, "secondDirectionOppositeDirection" : true, "secondDirectionDepth" : 114 * mm});
        }
    });
